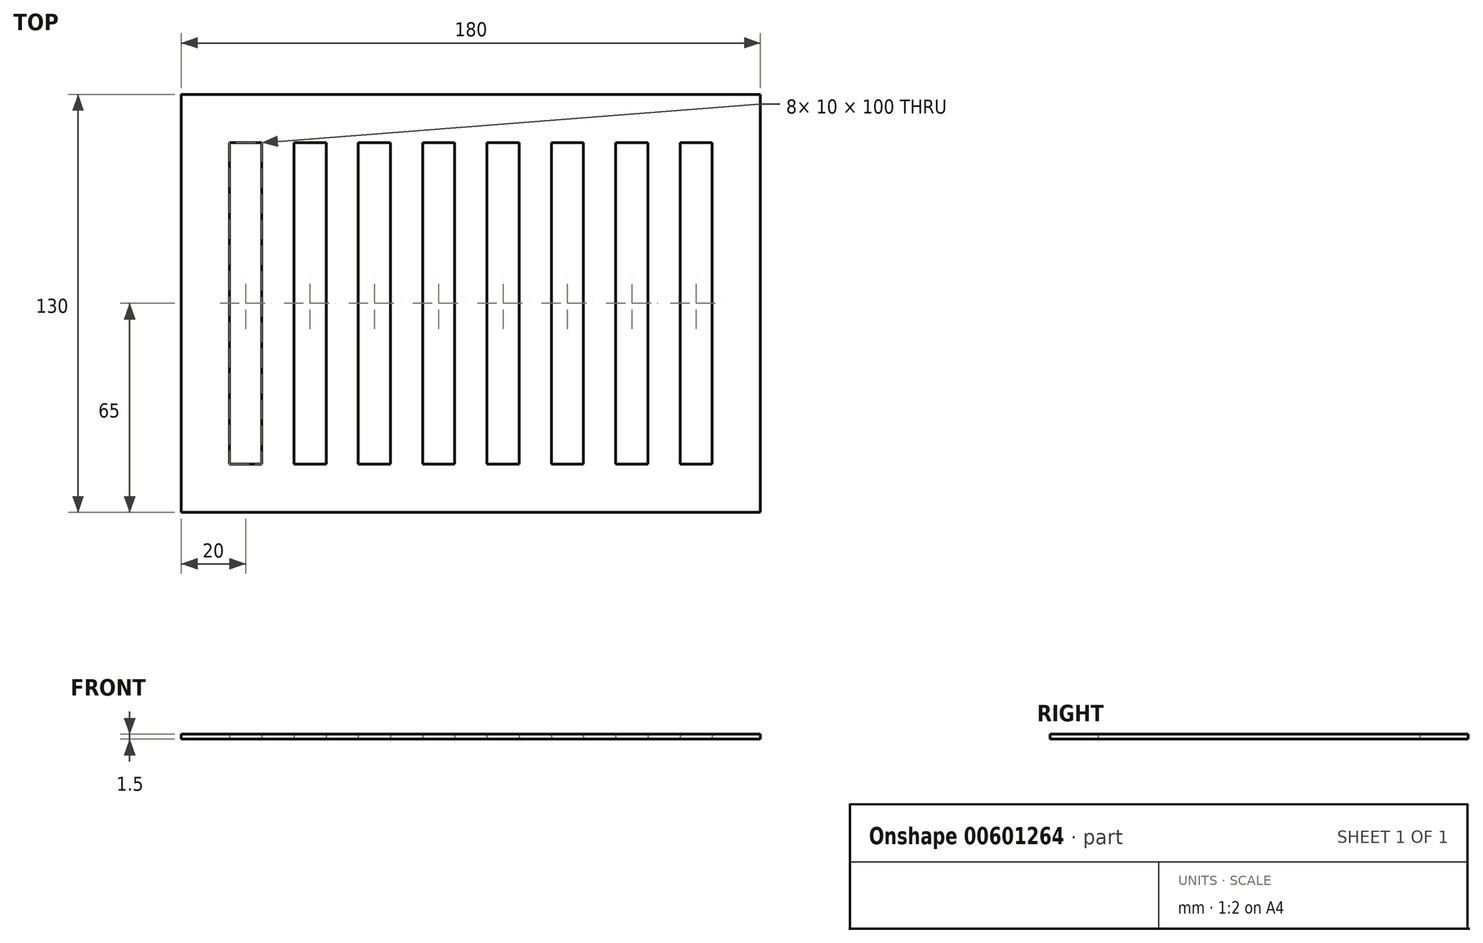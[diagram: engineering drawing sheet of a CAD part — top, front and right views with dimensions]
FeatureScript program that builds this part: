
annotation { "Feature Type Name" : "Feature", "Feature Type Description" : "" }
export const myFeature = defineFeature(function(context is Context, id is Id, definition is map)
    precondition{}
    {
        {
            var Q0;
            Q0=qCreatedBy(makeId("Top.planeOp"),FACE);
            var sketch = newSketch(context, id + "F0", { "sketchPlane" : qUnion([Q0])});
            skLineSegment(sketch, "E0.bottom", {"start": v(-90, 65) * mm, "end": v(90, 65) * mm});
            skLineSegment(sketch, "E0.top", {"start": v(-90, -65) * mm, "end": v(90, -65) * mm});
            skLineSegment(sketch, "E0.left", {"start": v(-90, 65) * mm, "end": v(-90, -65) * mm});
            skLineSegment(sketch, "E0.right", {"start": v(90, 65) * mm, "end": v(90, -65) * mm});
            skPoint(sketch, "E0.middle", {"position": v(0, 0) * mm});
            skLineSegment(sketch, "E1.bottom", {"start": v(-75, 50) * mm, "end": v(-65, 50) * mm});
            skLineSegment(sketch, "E1.top", {"start": v(-75, -50) * mm, "end": v(-65, -50) * mm});
            skLineSegment(sketch, "E1.left", {"start": v(-75, 50) * mm, "end": v(-75, -50) * mm});
            skLineSegment(sketch, "E1.right", {"start": v(-65, 50) * mm, "end": v(-65, -50) * mm});
            skLineSegment(sketch, "E2.1.0.0", {"start": v(-55, 50) * mm, "end": v(-55, -50) * mm});
            skLineSegment(sketch, "E2.1.0.1", {"start": v(-45, 50) * mm, "end": v(-45, -50) * mm});
            skLineSegment(sketch, "E2.1.0.2", {"start": v(-55, 50) * mm, "end": v(-45, 50) * mm});
            skLineSegment(sketch, "E2.1.0.3", {"start": v(-55, -50) * mm, "end": v(-45, -50) * mm});
            skLineSegment(sketch, "E2.2.0.0", {"start": v(-35, 50) * mm, "end": v(-35, -50) * mm});
            skLineSegment(sketch, "E2.2.0.1", {"start": v(-25, 50) * mm, "end": v(-25, -50) * mm});
            skLineSegment(sketch, "E2.2.0.2", {"start": v(-35, 50) * mm, "end": v(-25, 50) * mm});
            skLineSegment(sketch, "E2.2.0.3", {"start": v(-35, -50) * mm, "end": v(-25, -50) * mm});
            skLineSegment(sketch, "E2.3.0.0", {"start": v(-15, 50) * mm, "end": v(-15, -50) * mm});
            skLineSegment(sketch, "E2.3.0.1", {"start": v(-5, 50) * mm, "end": v(-5, -50) * mm});
            skLineSegment(sketch, "E2.3.0.2", {"start": v(-15, 50) * mm, "end": v(-5, 50) * mm});
            skLineSegment(sketch, "E2.3.0.3", {"start": v(-15, -50) * mm, "end": v(-5, -50) * mm});
            skLineSegment(sketch, "E2.4.0.0", {"start": v(5, 50) * mm, "end": v(5, -50) * mm});
            skLineSegment(sketch, "E2.4.0.1", {"start": v(15, 50) * mm, "end": v(15, -50) * mm});
            skLineSegment(sketch, "E2.4.0.2", {"start": v(5, 50) * mm, "end": v(15, 50) * mm});
            skLineSegment(sketch, "E2.4.0.3", {"start": v(5, -50) * mm, "end": v(15, -50) * mm});
            skLineSegment(sketch, "E2.5.0.0", {"start": v(25, 50) * mm, "end": v(25, -50) * mm});
            skLineSegment(sketch, "E2.5.0.1", {"start": v(35, 50) * mm, "end": v(35, -50) * mm});
            skLineSegment(sketch, "E2.5.0.2", {"start": v(25, 50) * mm, "end": v(35, 50) * mm});
            skLineSegment(sketch, "E2.5.0.3", {"start": v(25, -50) * mm, "end": v(35, -50) * mm});
            skLineSegment(sketch, "E2.6.0.0", {"start": v(45, 50) * mm, "end": v(45, -50) * mm});
            skLineSegment(sketch, "E2.6.0.1", {"start": v(55, 50) * mm, "end": v(55, -50) * mm});
            skLineSegment(sketch, "E2.6.0.2", {"start": v(45, 50) * mm, "end": v(55, 50) * mm});
            skLineSegment(sketch, "E2.6.0.3", {"start": v(45, -50) * mm, "end": v(55, -50) * mm});
            skLineSegment(sketch, "E2.7.0.0", {"start": v(65, 50) * mm, "end": v(65, -50) * mm});
            skLineSegment(sketch, "E2.7.0.1", {"start": v(75, 50) * mm, "end": v(75, -50) * mm});
            skLineSegment(sketch, "E2.7.0.2", {"start": v(65, 50) * mm, "end": v(75, 50) * mm});
            skLineSegment(sketch, "E2.7.0.3", {"start": v(65, -50) * mm, "end": v(75, -50) * mm});
            skLineSegment(sketch, "E2.direction1", {"start": v(-75, -50) * mm, "end": v(-55, -50) * mm, "construction": true});
            skSolve(sketch);
        }
        {
            var Q0;
            Q0 = qSketchRegion(id + "F0", true);
            extrude(context, id + "F1", {"entities" : qUnion([Q0]), "depth" : 1.5 * mm, "offsetDistance" : 25 * mm});
        }
    });
